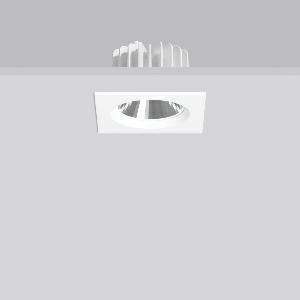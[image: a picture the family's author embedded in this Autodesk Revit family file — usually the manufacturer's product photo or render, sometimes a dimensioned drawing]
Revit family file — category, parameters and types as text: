
# Revit family: ledona_square_ip20_901792_002_15ef
name_source: partatom
category: Lighting Fixtures
units: mm (PartAtom-declared; Revit-internal decimal feet)

## family parameters
Cut with Voids When Loaded = No
Host = Face
Light Source = No
Part Type = Normal
Room Calculation Point = No
Round Connector Dimension = Use Diameter
Shared = No

## types (1)
- MultiLumen 1 (1 x LED Modul 930, 1500 lm, 3000)
    Apparent Load = 12 VA
    Approval mark = CE
    CIE Flux Codes = 96 100 100 100 100
    Color Rendering = 90
    Color Temperature = 3000
    Default Elevation = 1800 mm
    Description = Series: LEDONA square
Recessed LED downlight featuring advanced technology and sophisticated design. Housing: die-cast aluminium constructed as heat sink. Square cover plate: die-cast aluminium, powder coated. Round ceiling cut-out also with square types. MultiLumen: Luminous flux adjustable in different steps. Best colour rendering index Ra>90. Installation without tools thanks to spring fastening system. Connected converter included in separate gearbox. With connecting cable (L 250 mm). Suitable for through-wiring with separately available accessories. Through-wiring box (5 pole) available as accessory. 
Colour: white
Length: 130 mm
Width: 130 mm
Height: 3 mm
Cut-out diameter: 120 mm
Recess height: 79 mm
Luminaire: recess height: 79 mm
Lamp: LED
Socket: without socket
Colour temperature: 3000K
Colour rendering index (CRI): 90
System power: 12 W
Rated luminous flux: 1500 lm
Luminous efficiency: 125 lm/W
System power 2: 16 W
Rated luminous flux 2: 1950 lm
Luminous efficiency 2: 122 lm/W
System power 3: 19 W
Rated luminous flux 3: 2400 lm
Luminous efficiency 3: 126 lm/W
System power 4: 25 W
Rated luminous flux 4: 3000 lm
Luminous efficiency 4: 120 lm/W
Control gear: Regulated power supply
Protection class: II
Type of protection: IP 20
    Height = 0 mm  [stored 0 ft]
    Lamp = 1 x LED Modul 930
    Lamp Light Flux = 1500 lm
    Lamp count = 1
    Length = 130 mm
    Lifetime = 50000 h
    Luminous efficacy = 125 lm/W
    Manufacturer = RZB
    ModVariant = No
    Model = 901792.002
    Mounting Place = Ceiling
    Mounting Type = Recessed
    Number of Poles = 1
    OnlyDefault = Yes
    Power Factor = 1
    Product Name = LEDONA square IP20
    Product group = Recessed downlights
    ProductGroupID = 402
    Protection Class = Protection class II
    Protection Degree = IP 20
    RLX_Detail_Level = 1
    RLX_Emergency_Light_Flux = 0 lm
    RLX_Emergency_Type = 0
    RLX_Emergency_Type_DB = No
    RlxData = <blob elided: 30389 chars, md5=ac071b80>
    Socket = socket
    Standby Power = 0 W
    System Light Flux = 1500 lm
    System Power = 12 W
    Type Comments = MultiLumen 1
    Type Image = 901389.002.jpg
    URL = http://relux.com
    VarID = multilumen_1
    Voltage = 230 V
    Voltage Range = 220-240 V
    Weight = 0.00 kg
    Width = 130 mm

note: [stored X ft] marks values corroborated as IEEE doubles in the binary element streams (Revit-internal decimal feet)

## geometry (parser evidence)
native form markers: Blend x4, Sweep x10
no freeform markers — native parametric forms only
